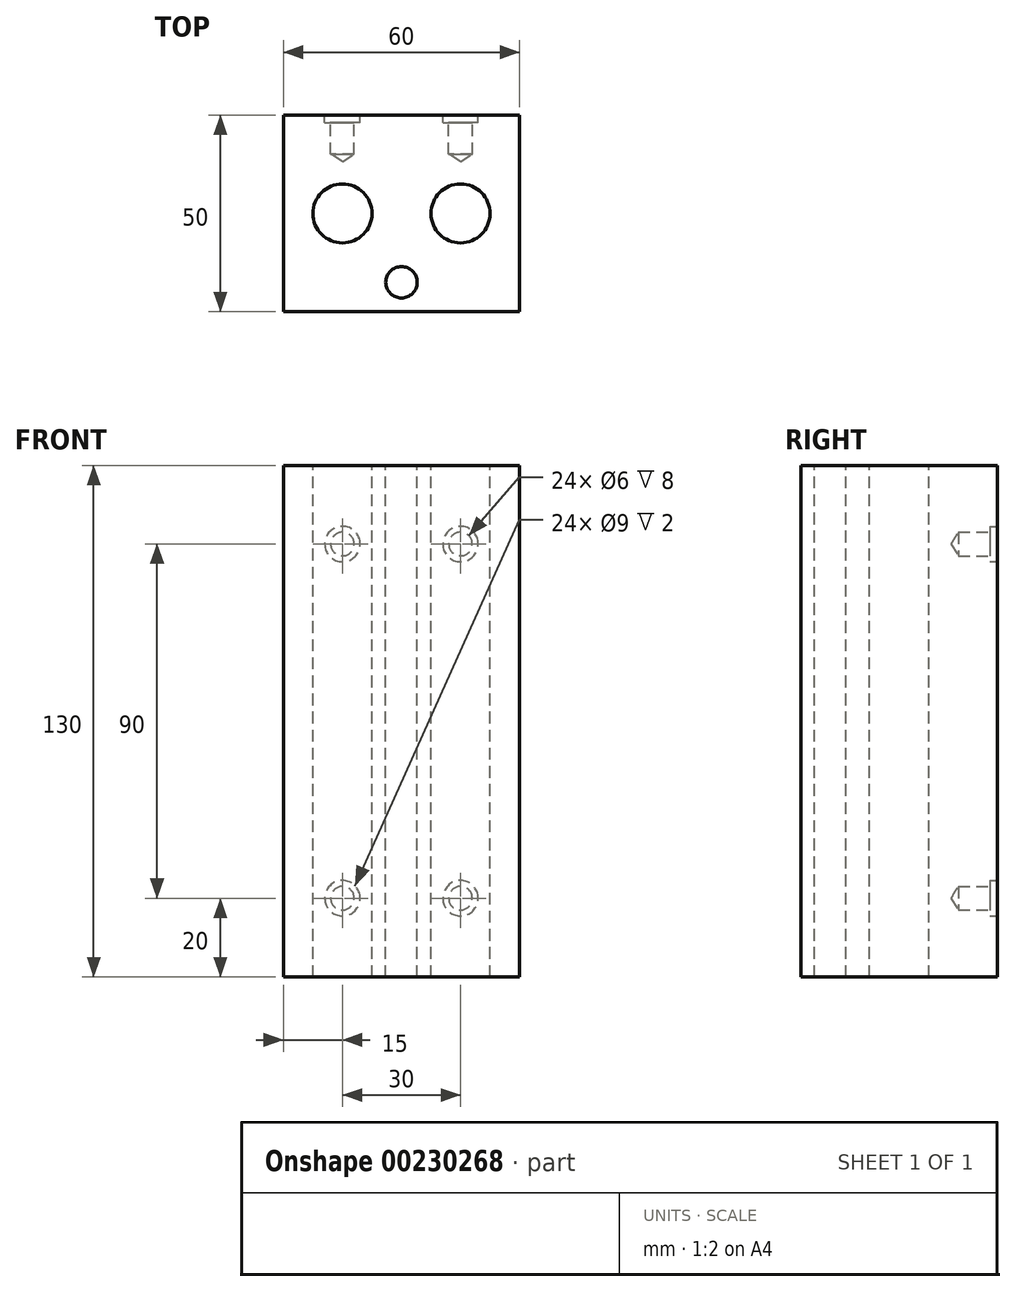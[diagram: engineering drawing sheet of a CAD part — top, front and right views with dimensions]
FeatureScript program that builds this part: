
annotation { "Feature Type Name" : "Feature", "Feature Type Description" : "" }
export const myFeature = defineFeature(function(context is Context, id is Id, definition is map)
    precondition{}
    {
        {
            var Q0;
            Q0=qCreatedBy(makeId("Front.planeOp"),FACE);
            var sketch = newSketch(context, id + "F0", { "sketchPlane" : qUnion([Q0])});
            skLineSegment(sketch, "E0.bottom", {"start": v(30, -65) * mm, "end": v(-30, -65) * mm});
            skLineSegment(sketch, "E0.top", {"start": v(30, 65) * mm, "end": v(-30, 65) * mm});
            skLineSegment(sketch, "E0.left", {"start": v(30, -65) * mm, "end": v(30, 65) * mm});
            skLineSegment(sketch, "E0.right", {"start": v(-30, -65) * mm, "end": v(-30, 65) * mm});
            skPoint(sketch, "E0.middle", {"position": v(0, 0) * mm});
            skSolve(sketch);
        }
        {
            var Q0;
            Q0=makeQuery(id+"F0.imprint","IMPRINT",FACE,{"disambiguationData":[TD([[makeQuery(id+"F0.imprint","IMPRINT",EDGE,{"derivedFrom":sQuery(id+"F0.wireOp",EDGE,"E0.bottom")}),-1.0]])]});
            extrude(context, id + "F1", {"entities" : qUnion([Q0]), "endBound" : BoundingType.SYMMETRIC, "depth" : 50 * mm});
        }
        {
            var Q0;
            Q0=makeQuery(id+"F1.opExtrude","SWEPT_FACE",FACE,{"disambiguationData":[OSD([sQuery(id+"F0.wireOp",EDGE,"E0.top")])]});
            var sketch = newSketch(context, id + "F2", { "sketchPlane" : qUnion([Q0])});
            skCircle(sketch, "E1", {"center": v(-15, 0) * mm, "radius": 7.5 * mm});
            skCircle(sketch, "E2", {"center": v(15, 0) * mm, "radius": 7.5 * mm});
            skCircle(sketch, "E3", {"center": v(0, -17.5) * mm, "radius": 4 * mm});
            skSolve(sketch);
        }
        {
            var Q0;
            Q0=makeQuery(id+"F2.imprint","IMPRINT",FACE,{"disambiguationData":[TD([[makeQuery(id+"F2.imprint","IMPRINT",EDGE,{"derivedFrom":sQuery(id+"F2.wireOp",EDGE,"E1")}),1.0]])]});
            var Q1;
            Q1=makeQuery(id+"F2.imprint","IMPRINT",FACE,{"disambiguationData":[TD([[makeQuery(id+"F2.imprint","IMPRINT",EDGE,{"derivedFrom":sQuery(id+"F2.wireOp",EDGE,"E2")}),1.0]])]});
            var Q2;
            Q2=makeQuery(id+"F2.imprint","IMPRINT",FACE,{"disambiguationData":[TD([[makeQuery(id+"F2.imprint","IMPRINT",EDGE,{"derivedFrom":sQuery(id+"F2.wireOp",EDGE,"E3")}),1.0]])]});
            extrude(context, id + "F3", {"entities" : qUnion([Q0, Q1, Q2]), "operationType" : NewBodyOperationType.REMOVE, "endBound" : BoundingType.THROUGH_ALL, "oppositeDirection" : true, "depth" : 149.6 * mm});
        }
        {
            var Q0;
            Q0=makeQuery(id+"F1.opExtrude","CAP_FACE",FACE,{"disambiguationData":[OSD([sQuery(id+"F0.wireOp",EDGE,"E0.bottom"),sQuery(id+"F0.wireOp",EDGE,"E0.top"),sQuery(id+"F0.wireOp",EDGE,"E0.left"),sQuery(id+"F0.wireOp",EDGE,"E0.right")])],"isStart":true});
            var sketch = newSketch(context, id + "F4", { "sketchPlane" : qUnion([Q0])});
            skPoint(sketch, "E4", {"position": v(-15, 45) * mm});
            skPoint(sketch, "E5", {"position": v(15, 45) * mm});
            skPoint(sketch, "E6", {"position": v(15, -45) * mm});
            skPoint(sketch, "E7", {"position": v(-15, -45) * mm});
            skSolve(sketch);
        }
        {
            var Q0;
            Q0=sQuery(id+"F4.wireOp",VERTEX,"E4");
            var Q1;
            Q1=sQuery(id+"F4.wireOp",VERTEX,"E5");
            var Q2;
            Q2=sQuery(id+"F4.wireOp",VERTEX,"E6");
            var Q3;
            Q3=sQuery(id+"F4.wireOp",VERTEX,"E7");
            var Q4;
            Q4=makeQuery(id+"F1.opExtrude","SWEPT_BODY",BODY,{"disambiguationData":[OSD([sQuery(id+"F0.wireOp",EDGE,"E0.bottom"),sQuery(id+"F0.wireOp",EDGE,"E0.top"),sQuery(id+"F0.wireOp",EDGE,"E0.left"),sQuery(id+"F0.wireOp",EDGE,"E0.right")])]});
            hole(context, id + "F5", {"style" : HoleStyle.C_BORE, "endStyle" : HoleEndStyle.BLIND, "holeDiameter" : 6 * mm, "cBoreDiameter" : 9 * mm, "cBoreDepth" : 2 * mm, "holeDepth" : 10 * mm, "locations" : qUnion([Q0, Q1, Q2, Q3]), "scope" : qUnion([Q4])});
        }
    });
